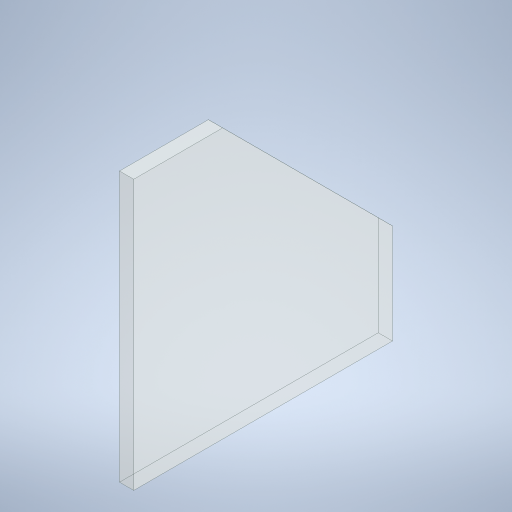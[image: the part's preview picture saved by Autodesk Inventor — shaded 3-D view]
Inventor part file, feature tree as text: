
AUTODESK INVENTOR PART (.ipt)
format: ipt  version: 2024 (Build 280153000, 153)  size: 230,400 bytes
history: native  units: in
note: dims shown in document units (in); Inventor stores cm internally (conversion verified against a paired STEP export)
features: extrude x1, sketch x1
ambient origin geometry x8: Origin, YZ Plane, XZ Plane, XY Plane, X Axis, Y Axis, Z Axis, Center Point
bodies: Solid1 (feature_tree)
feature tree (2):
  extrude  "Extrusion1"  Depth=0.75in
  sketch  "Sketch1"  dims[d0=91.5in d1=96.0in d2=36.0in d3=135.0deg d4=5.0in d5=0.0in d6=0.75in d7=0.75in d8=0.75in]
